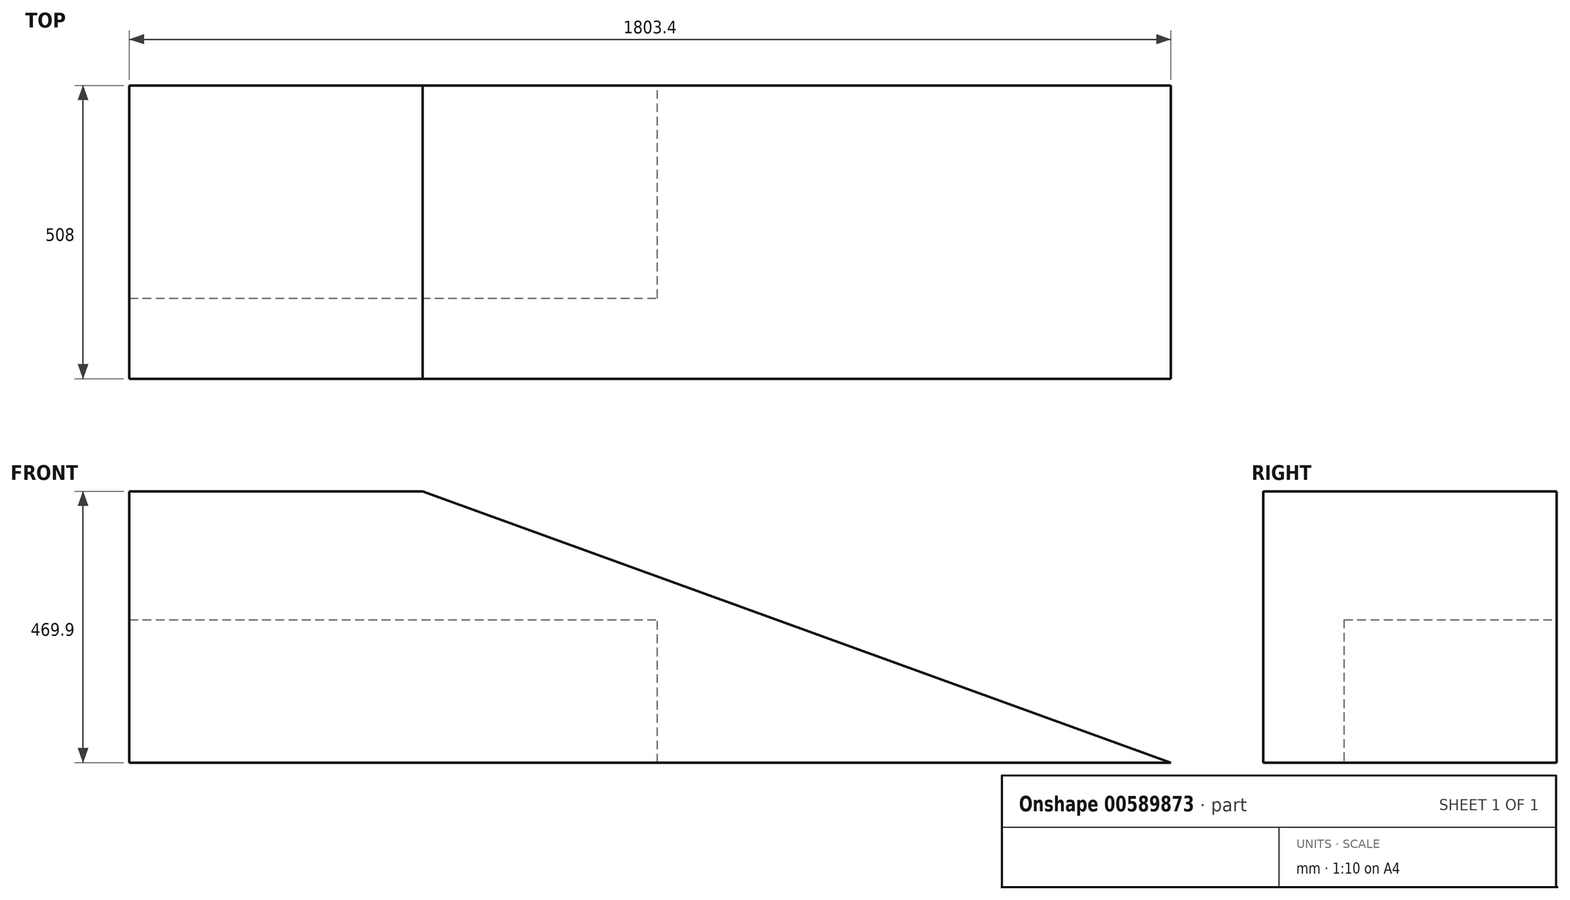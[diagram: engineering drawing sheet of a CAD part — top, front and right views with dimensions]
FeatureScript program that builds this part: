
annotation { "Feature Type Name" : "Feature", "Feature Type Description" : "" }
export const myFeature = defineFeature(function(context is Context, id is Id, definition is map)
    precondition{}
    {
        {
            var Q0;
            Q0=qCreatedBy(makeId("Front.planeOp"),FACE);
            var sketch = newSketch(context, id + "F0", { "sketchPlane" : qUnion([Q0])});
            skLineSegment(sketch, "E0.bottom", {"start": v(158.22, 0) * mm, "end": v(666.22, 0) * mm});
            skLineSegment(sketch, "E0.top", {"start": v(158.22, -469.9) * mm, "end": v(1961.62, -469.9) * mm});
            skLineSegment(sketch, "E0.left", {"start": v(158.22, 0) * mm, "end": v(158.22, -469.9) * mm});
            skLineSegment(sketch, "E1", {"start": v(1961.62, -469.9) * mm, "end": v(666.22, 0) * mm});
            skSolve(sketch);
        }
        {
            var Q0;
            Q0 = qSketchRegion(id + "F0", true);
            extrude(context, id + "F1", {"entities" : qUnion([Q0]), "depth" : 508 * mm, "offsetDistance" : 25.4 * mm});
        }
        {
            var Q0;
            Q0=makeQuery(id+"F1.opExtrude","CAP_FACE",FACE,{"disambiguationData":[OSD([sQuery(id+"F0.wireOp",EDGE,"E0.bottom"),sQuery(id+"F0.wireOp",EDGE,"E0.top"),sQuery(id+"F0.wireOp",EDGE,"E0.left"),sQuery(id+"F0.wireOp",EDGE,"E1")])],"isStart":true});
            var sketch = newSketch(context, id + "F2", { "sketchPlane" : qUnion([Q0])});
            skLineSegment(sketch, "E2.bottom", {"start": v(-158.22, -469.9) * mm, "end": v(-1072.62, -469.9) * mm});
            skLineSegment(sketch, "E2.top", {"start": v(-158.22, -222.25) * mm, "end": v(-1072.62, -222.25) * mm});
            skLineSegment(sketch, "E2.left", {"start": v(-158.22, -469.9) * mm, "end": v(-158.22, -222.25) * mm});
            skLineSegment(sketch, "E2.right", {"start": v(-1072.62, -469.9) * mm, "end": v(-1072.62, -222.25) * mm});
            skSolve(sketch);
        }
        {
            var Q0;
            Q0=makeQuery(id+"F2.imprint","IMPRINT",FACE,{"disambiguationData":[TD([[makeQuery(id+"F2.imprint","IMPRINT",EDGE,{"derivedFrom":sQuery(id+"F2.wireOp",EDGE,"E2.bottom")}),-1.0]])]});
            extrude(context, id + "F3", {"entities" : qUnion([Q0]), "operationType" : NewBodyOperationType.REMOVE, "oppositeDirection" : true, "depth" : 368.3 * mm, "offsetDistance" : 25.4 * mm});
        }
    });
